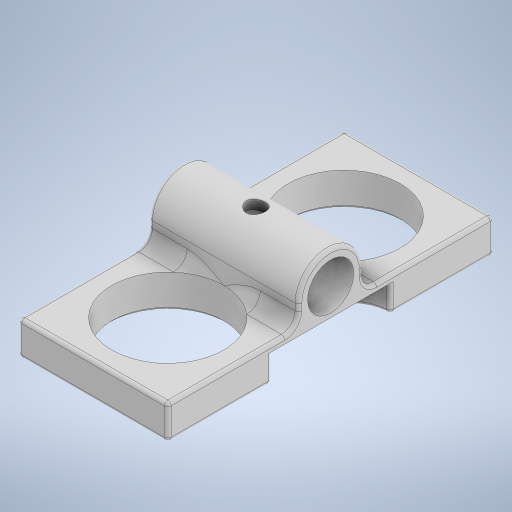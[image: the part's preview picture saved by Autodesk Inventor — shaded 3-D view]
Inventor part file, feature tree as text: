
AUTODESK INVENTOR PART (.ipt)
format: ipt  version: 2024.2 (Build 282272000, 272)  size: 428,544 bytes
history: native  units: mm
features: extrude x5, sketch x4, fillet x3, chamfer x1, plane x1
ambient origin geometry x8: Origin, YZ Plane, XZ Plane, XY Plane, X Axis, Y Axis, Z Axis, Center Point
bodies: Solid1 (feature_tree)
feature tree (14):
  extrude  "Extrusion1"  Depth=26.0mm
  sketch  "Sketch2"  dims[d2=13.0mm d3=11.0mm]
  extrude  "Extrusion2"  Depth=11.0mm
  extrude  "Extrusion3"  Depth=11.0mm
  extrude  "Extrusion4"  Depth=10.0mm TaperAngle=0.0deg
  fillet  "Fillet1"  Radius=6.8mm
  fillet  "Fillet2"  Radius=9.5mm
  fillet  "Fillet3"  Radius=8.0mm
  chamfer  "Chamfer1"  Distance=3.0mm
  plane  "Work Plane1"
  extrude  "Extrusion5"  TaperAngle=0.0deg  [1 undecoded]
  sketch  "Sketch1"  dims[d0=16.5mm d1=26.0mm]
  sketch  "Sketch3"  dims[d4=11.0mm d5=11.0mm]
  sketch  "Sketch4"  dims[d6=11.0mm d7=5.0mm d8=0.0mm d9=6.8mm d10=9.5mm d11=8.0mm d12=3.0mm d13=0.0mm d14=0.0mm d15=0.0mm d18=12.5mm d19=5.0mm d20=4.0mm d21=0.0mm d22=2.0mm d23=0.5mm d24=0.5mm d25=0.5mm d26=2.0mm d27=45.0deg d28=10.0mm d29=2.8mm d30=2.0mm d31=0.0mm]
note: 1 required parameter value undecoded (feature->parameter linkage not recoverable at this tier; creation-order binding heuristic only, values carry confidence <= 0.55)
